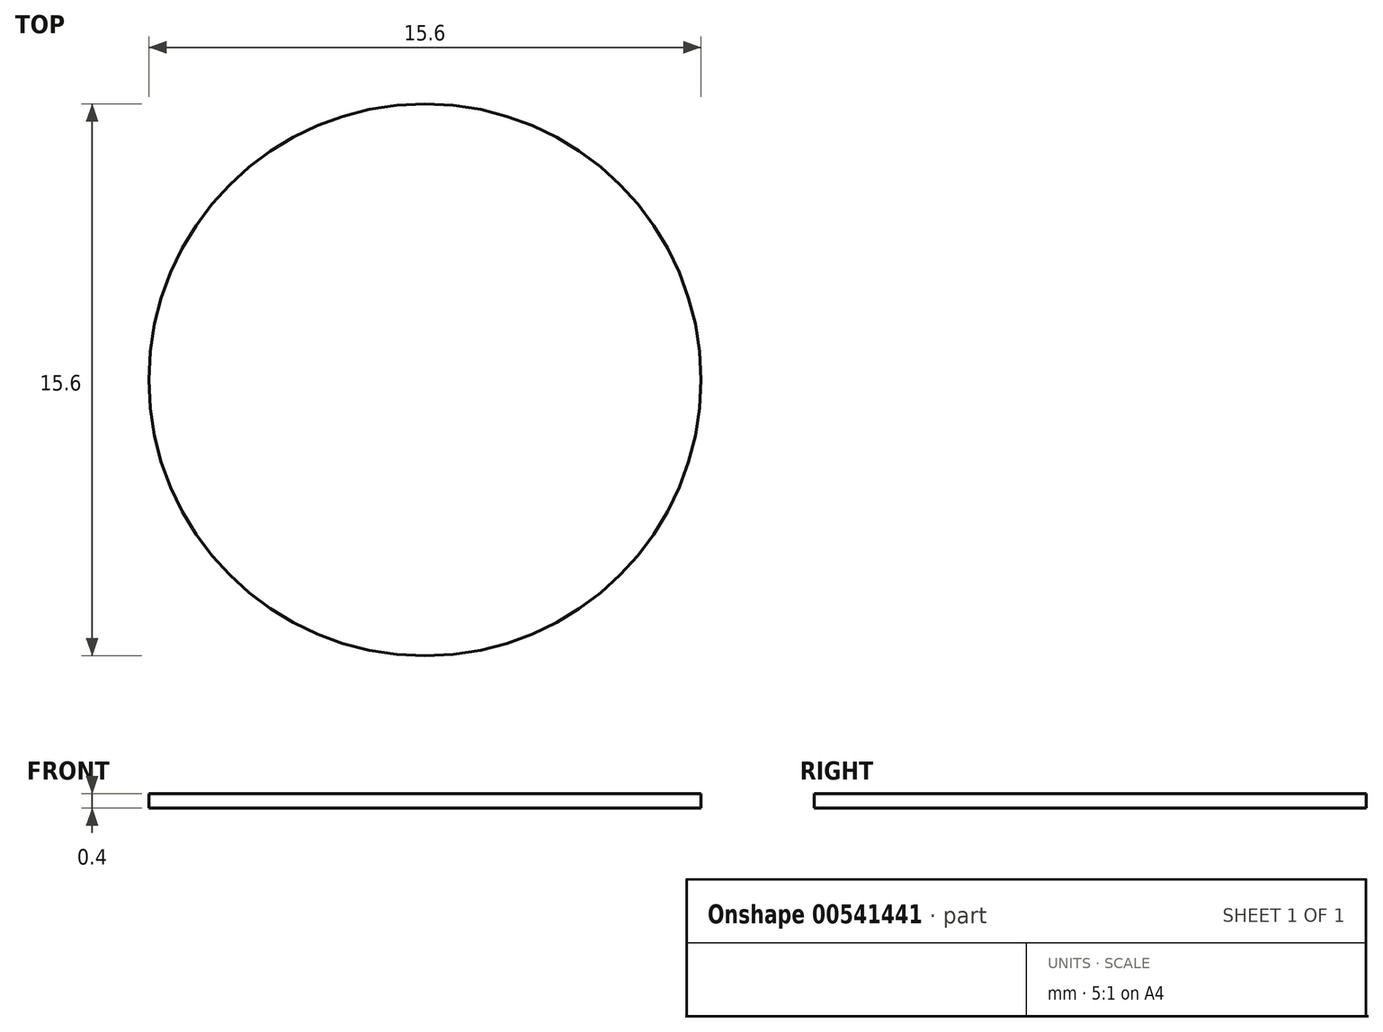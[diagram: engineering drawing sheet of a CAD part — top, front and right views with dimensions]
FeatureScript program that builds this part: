
annotation { "Feature Type Name" : "Feature", "Feature Type Description" : "" }
export const myFeature = defineFeature(function(context is Context, id is Id, definition is map)
    precondition{}
    {
        {
            var Q0;
            Q0=qCreatedBy(makeId("Top.planeOp"),FACE);
            var sketch = newSketch(context, id + "F0", { "sketchPlane" : qUnion([Q0])});
            skCircle(sketch, "E0", {"center": v(0, 0) * mm, "radius": 7.8 * mm});
            skSolve(sketch);
        }
        {
            var Q0;
            Q0=makeQuery(id+"F0.imprint","IMPRINT",FACE,{"disambiguationData":[TD([[makeQuery(id+"F0.imprint","IMPRINT",EDGE,{"derivedFrom":sQuery(id+"F0.wireOp",EDGE,"E0")}),1.0]])]});
            extrude(context, id + "F1", {"entities" : qUnion([Q0]), "depth" : .4 * mm, "offsetDistance" : 25 * mm});
        }
        {
            var Q0;
            Q0=makeQuery(id+"F1.opExtrude","CAP_FACE",FACE,{"disambiguationData":[OSD([sQuery(id+"F0.wireOp",EDGE,"E0")])],"isStart":false});
            var sketch = newSketch(context, id + "F2", { "sketchPlane" : qUnion([Q0])});
            skArc(sketch, "E1", {"start": v(-4.5, 3.86) * mm, "mid": v(-3.88, -4.5) * mm, "end": v(4.48, -3.9) * mm});
            skLineSegment(sketch, "E2", {"start": v(-4.5, 3.86) * mm, "end": v(4.48, -3.9) * mm});
            skSolve(sketch);
        }
    });
